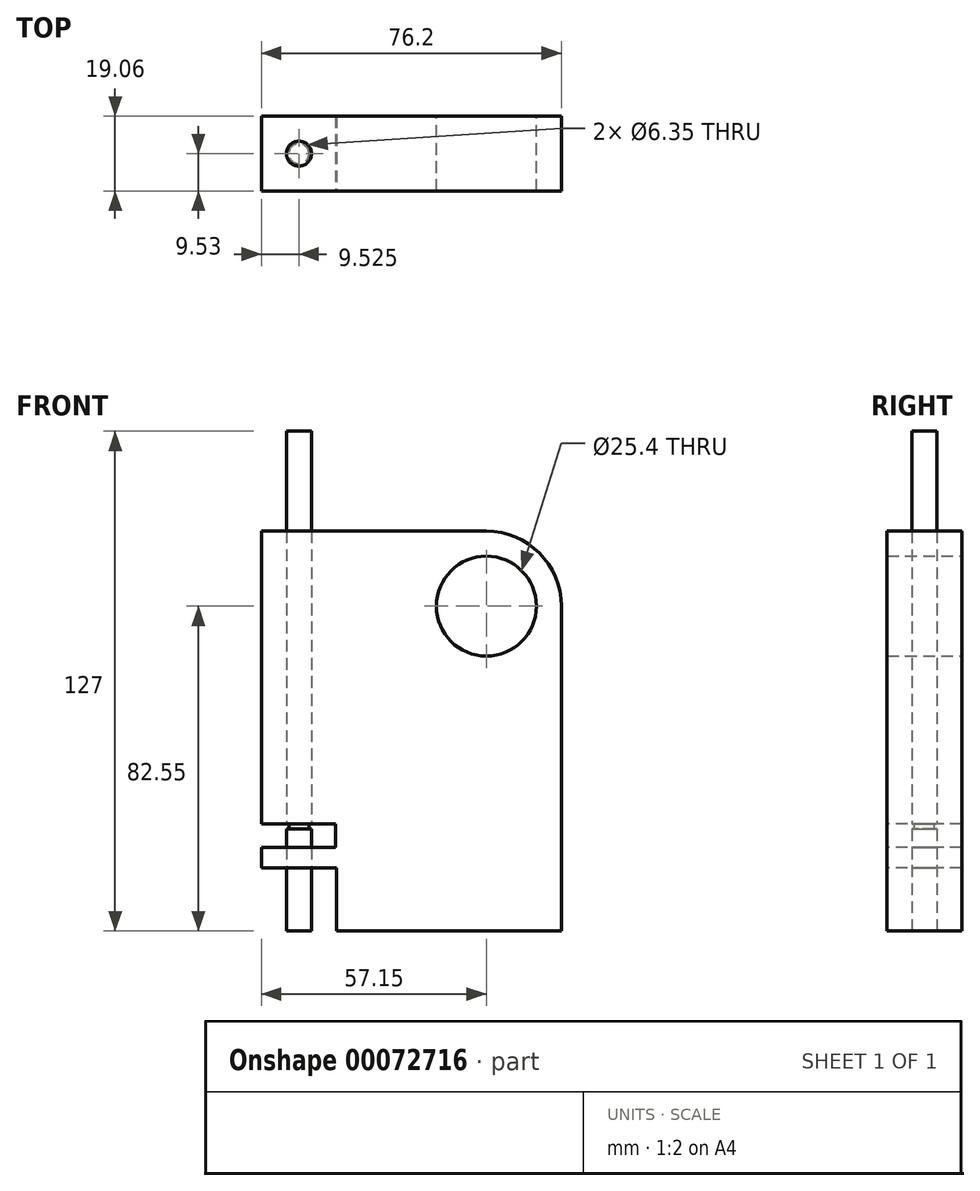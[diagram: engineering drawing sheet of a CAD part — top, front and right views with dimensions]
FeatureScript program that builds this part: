
annotation { "Feature Type Name" : "Feature", "Feature Type Description" : "" }
export const myFeature = defineFeature(function(context is Context, id is Id, definition is map)
    precondition{}
    {
        {
            var Q0;
            Q0=qCreatedBy(makeId("Front.planeOp"),FACE);
            var sketch = newSketch(context, id + "F0", { "sketchPlane" : qUnion([Q0])});
            skLineSegment(sketch, "E0.bottom", {"start": v(0, 0) * mm, "end": v(76.2, 0) * mm});
            skLineSegment(sketch, "E0.top", {"start": v(0, 101.6) * mm, "end": v(57.15, 101.6) * mm});
            skLineSegment(sketch, "E0.left", {"start": v(0, 0) * mm, "end": v(0, 101.6) * mm});
            skLineSegment(sketch, "E0.right", {"start": v(76.2, 0) * mm, "end": v(76.2, 82.55) * mm});
            skPoint(sketch, "E1.visualSharp", {"position": v(76.2, 101.6) * mm});
            skArc(sketch, "E1.filletArc", {"start": v(76.2, 82.55) * mm, "mid": v(70.62, 96.02) * mm, "end": v(57.15, 101.6) * mm});
            skCircle(sketch, "E2", {"center": v(57.15, 82.55) * mm, "radius": 12.7 * mm});
            skSolve(sketch);
        }
        {
            var Q0;
            Q0=makeQuery(id+"F0.imprint","IMPRINT",FACE,{"disambiguationData":[TD([[makeQuery(id+"F0.imprint","IMPRINT",EDGE,{"derivedFrom":sQuery(id+"F0.wireOp",EDGE,"E0.bottom")}),1.0]])]});
            extrude(context, id + "F1", {"entities" : qUnion([Q0]), "endBound" : BoundingType.SYMMETRIC, "depth" : 19.05 * mm});
        }
        {
            var Q0;
            Q0=qCreatedBy(makeId("Front.planeOp"),FACE);
            var sketch = newSketch(context, id + "F2", { "sketchPlane" : qUnion([Q0])});
            skLineSegment(sketch, "E3.bottom", {"start": v(0, 0) * mm, "end": v(19.05, 0) * mm});
            skLineSegment(sketch, "E3.top", {"start": v(0, 16) * mm, "end": v(19.05, 16) * mm});
            skLineSegment(sketch, "E3.left", {"start": v(0, 0) * mm, "end": v(0, 16) * mm});
            skLineSegment(sketch, "E3.right", {"start": v(19.05, 0) * mm, "end": v(19.05, 16) * mm});
            skLineSegment(sketch, "E4.bottom", {"start": v(0, 27.24) * mm, "end": v(18.88, 27.24) * mm});
            skLineSegment(sketch, "E4.top", {"start": v(0, 21.2) * mm, "end": v(18.88, 21.2) * mm});
            skLineSegment(sketch, "E4.left", {"start": v(0, 27.24) * mm, "end": v(0, 21.2) * mm});
            skLineSegment(sketch, "E4.right", {"start": v(18.88, 27.24) * mm, "end": v(18.88, 21.2) * mm});
            skSolve(sketch);
        }
        {
            var Q0;
            Q0 = qSketchRegion(id + "F2", true);
            extrude(context, id + "F3", {"entities" : qUnion([Q0]), "operationType" : NewBodyOperationType.REMOVE, "endBound" : BoundingType.THROUGH_ALL, "oppositeDirection" : true, "depth" : 25.4 * mm, "hasSecondDirection" : true, "secondDirectionBound" : SecondDirectionBoundingType.THROUGH_ALL, "secondDirectionOppositeDirection" : false, "secondDirectionDepth" : 25.4 * mm});
        }
        {
            var Q0;
            Q0=qCreatedBy(makeId("Top.planeOp"),FACE);
            var sketch = newSketch(context, id + "F4", { "sketchPlane" : qUnion([Q0])});
            skCircle(sketch, "E5", {"center": v(9.52, 0) * mm, "radius": 3.18 * mm});
            skLineSegment(sketch, "E6", {"start": v(0, 0) * mm, "end": v(9.52, 0) * mm});
            skLineSegment(sketch, "E7", {"start": v(9.52, 9.53) * mm, "end": v(9.52, 0) * mm});
            skSolve(sketch);
        }
        {
            var Q0;
            Q0 = qSketchRegion(id + "F4", true);
            extrude(context, id + "F5", {"entities" : qUnion([Q0]), "operationType" : NewBodyOperationType.REMOVE, "endBound" : BoundingType.THROUGH_ALL, "depth" : 25.4 * mm});
        }
        {
            var Q0;
            Q0 = qSketchRegion(id + "F4", true);
            extrude(context, id + "F6", {"entities" : qUnion([Q0]), "depth" : 127 * mm});
        }
        {
            var Q0;
            Q0=makeQuery(id+"F3.boolean.opBoolean","COPY",FACE,{"derivedFrom":makeQuery(id+"F3.opExtrude","SWEPT_FACE",FACE,{"disambiguationData":[OSD([sQuery(id+"F2.wireOp",EDGE,"E4.bottom")])]})});
            var sketch = newSketch(context, id + "F7", { "sketchPlane" : qUnion([Q0])});
            skCircle(sketch, "E8", {"center": v(9.52, 0) * mm, "radius": 2.54 * mm});
            skCircle(sketch, "E9.0", {"center": v(9.52, 0) * mm, "radius": 3.18 * mm});
            skSolve(sketch);
        }
        {
            var Q0;
            Q0 = qSketchRegion(id + "F7", true);
            extrude(context, id + "F8", {"entities" : qUnion([Q0]), "operationType" : NewBodyOperationType.REMOVE, "depth" : 1.27 * mm});
        }
    });
